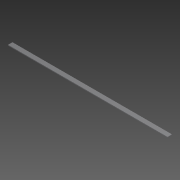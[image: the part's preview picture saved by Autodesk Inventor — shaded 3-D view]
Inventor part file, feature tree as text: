
AUTODESK INVENTOR PART (.ipt)
format: ipt  version: 2013 (Build 170138000, 138)  size: 65,024 bytes
history: native  units: in
note: dims shown in document units (in); Inventor stores cm internally (conversion verified against a paired STEP export)
features: extrude x1, sketch x1
ambient origin geometry x8: Origin, YZ Plane, XZ Plane, XY Plane, X Axis, Y Axis, Z Axis, Center Point
bodies: Solid1 (feature_tree)
feature tree (2):
  extrude  "Extrusion1"  Depth=1.5in
  sketch  "Sketch1"  dims[d0=53.5in d1=1.5in d2=0.25in d3=0.0in]
